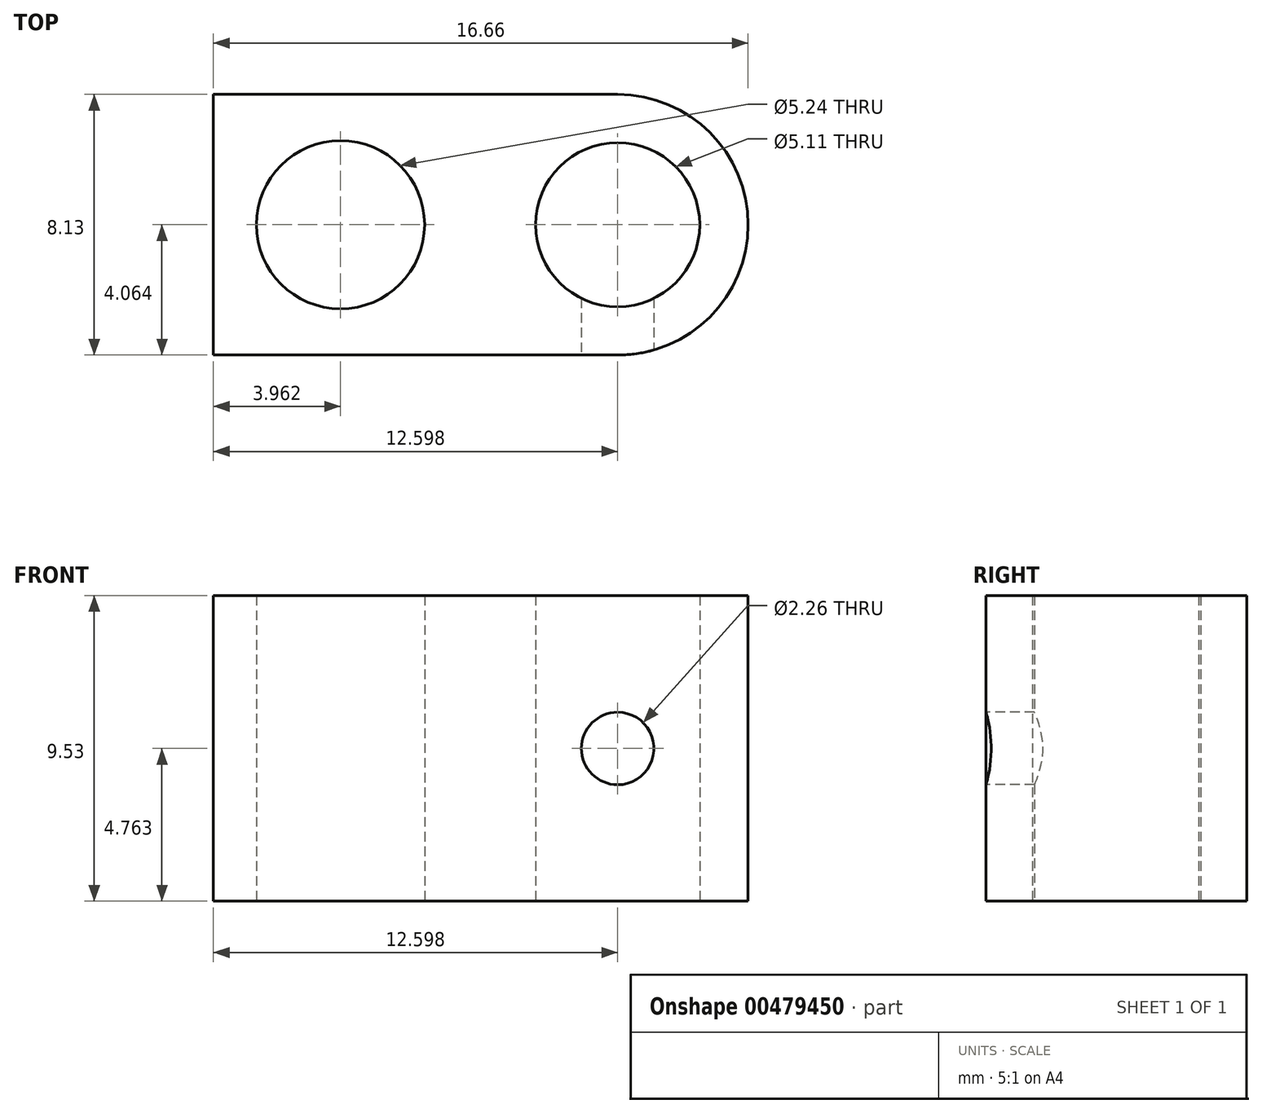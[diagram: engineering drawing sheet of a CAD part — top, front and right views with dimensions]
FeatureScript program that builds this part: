
annotation { "Feature Type Name" : "Feature", "Feature Type Description" : "" }
export const myFeature = defineFeature(function(context is Context, id is Id, definition is map)
    precondition{}
    {
        {
            var Q0;
            Q0=qCreatedBy(makeId("Top.planeOp"),FACE);
            var sketch = newSketch(context, id + "F0", { "sketchPlane" : qUnion([Q0])});
            skLineSegment(sketch, "E0.bottom", {"start": v(0, 0) * mm, "end": v(12.6, 0) * mm});
            skLineSegment(sketch, "E0.top", {"start": v(0, 8.13) * mm, "end": v(12.6, 8.13) * mm});
            skLineSegment(sketch, "E0.left", {"start": v(0, 0) * mm, "end": v(0, 8.13) * mm});
            skCircle(sketch, "E1", {"center": v(3.96, 4.06) * mm, "radius": 2.62 * mm});
            skPoint(sketch, "E1.centerSnap0", {"position": v(0, 4.06) * mm});
            skCircle(sketch, "E2", {"center": v(12.6, 4.06) * mm, "radius": 2.56 * mm});
            skArc(sketch, "E3", {"start": v(12.6, 0) * mm, "mid": v(16.66, 4.06) * mm, "end": v(12.6, 8.13) * mm});
            skSolve(sketch);
        }
        {
            var Q0;
            Q0=makeQuery(id+"F0.imprint","IMPRINT",FACE,{"disambiguationData":[TD([[makeQuery(id+"F0.imprint","IMPRINT",EDGE,{"derivedFrom":sQuery(id+"F0.wireOp",EDGE,"E0.bottom")}),1.0]])]});
            extrude(context, id + "F1", {"entities" : qUnion([Q0]), "depth" : 9.52 * mm});
        }
        {
            var Q0;
            Q0=makeQuery(id+"F1.opExtrude","SWEPT_FACE",FACE,{"disambiguationData":[OSD([sQuery(id+"F0.wireOp",EDGE,"E0.bottom")])]});
            var sketch = newSketch(context, id + "F2", { "sketchPlane" : qUnion([Q0])});
            skCircle(sketch, "E4", {"center": v(12.6, 4.76) * mm, "radius": 1.13 * mm});
            skSolve(sketch);
        }
        {
            var Q0;
            {var subQ0=sQuery(id+"F2.wireOp",EDGE,"E4");var subQ1=makeQuery(id+"F1.opExtrude","SWEPT_EDGE",EDGE,{"disambiguationData":[OSD([sQuery(id+"F0.wireOp",EDGE,"E0.bottom"),sQuery(id+"F0.wireOp",EDGE,"E3")])]});var subQ2=makeQuery(id+"F2.imprint","INTERSECT",VERTEX,{"disambiguationData":[OD(0.0)],"derivedFrom":[subQ1,subQ0]});Q0=makeQuery(id+"F2.imprint","IMPRINT",FACE,{"disambiguationData":[TD([[makeQuery(id+"F2.imprint","IMPRINT",EDGE,{"disambiguationData":[TD([[subQ2,1.0]])],"derivedFrom":subQ0}),1.0]])]});}
            var Q1;
            {var subQ0=sQuery(id+"F2.wireOp",EDGE,"E4");var subQ1=makeQuery(id+"F1.opExtrude","SWEPT_EDGE",EDGE,{"disambiguationData":[OSD([sQuery(id+"F0.wireOp",EDGE,"E0.bottom"),sQuery(id+"F0.wireOp",EDGE,"E3")])]});var subQ2=makeQuery(id+"F2.imprint","INTERSECT",VERTEX,{"disambiguationData":[OD(0.0)],"derivedFrom":[subQ1,subQ0]});Q1=makeQuery(id+"F2.imprint","IMPRINT",FACE,{"disambiguationData":[TD([[makeQuery(id+"F2.imprint","IMPRINT",EDGE,{"disambiguationData":[TD([[subQ2,-1.0]])],"derivedFrom":subQ0}),1.0]])]});}
            extrude(context, id + "F3", {"entities" : qUnion([Q0, Q1]), "operationType" : NewBodyOperationType.REMOVE, "endBound" : BoundingType.UP_TO_NEXT, "oppositeDirection" : true, "depth" : 25.4 * mm});
        }
    });
